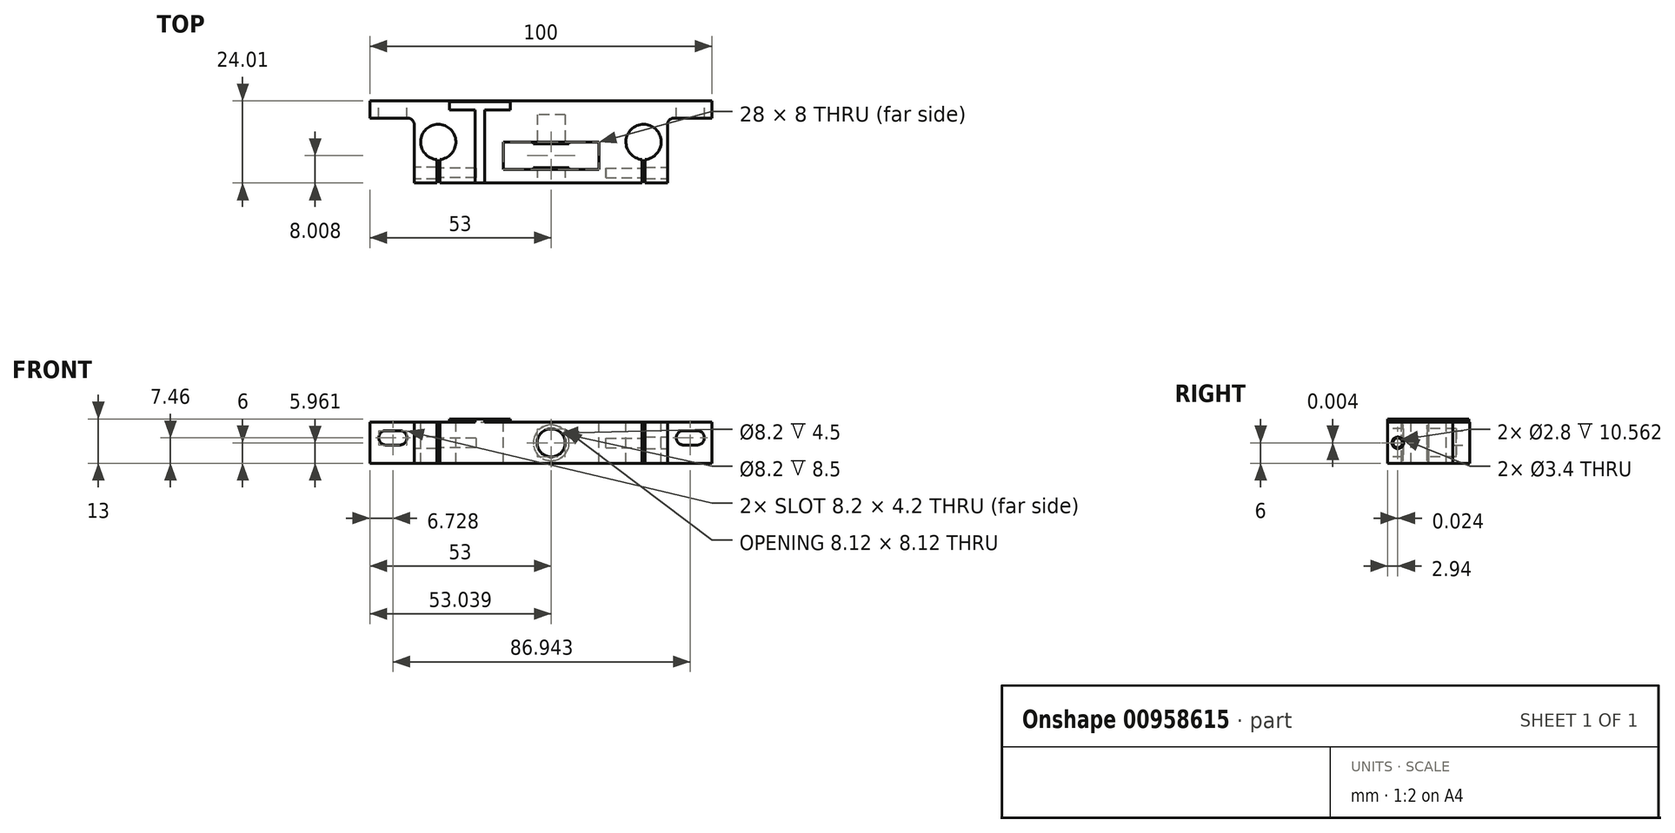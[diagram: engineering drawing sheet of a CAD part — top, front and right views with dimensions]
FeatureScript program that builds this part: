
annotation { "Feature Type Name" : "Feature", "Feature Type Description" : "" }
export const myFeature = defineFeature(function(context is Context, id is Id, definition is map)
    precondition{}
    {
        {
            var Q0;
            Q0=qCreatedBy(makeId("Top.planeOp"),FACE);
            var sketch = newSketch(context, id + "F0", { "sketchPlane" : qUnion([Q0])});
            skLineSegment(sketch, "E0", {"start": v(-46.35, 12.3) * mm, "end": v(53.65, 12.3) * mm});
            skLineSegment(sketch, "E1", {"start": v(53.65, 12.3) * mm, "end": v(53.65, 7.3) * mm});
            skLineSegment(sketch, "E2", {"start": v(53.65, 7.3) * mm, "end": v(40.65, 7.3) * mm});
            skLineSegment(sketch, "E3", {"start": v(40.65, 7.3) * mm, "end": v(40.65, -11.7) * mm});
            skLineSegment(sketch, "E4", {"start": v(40.65, -11.7) * mm, "end": v(-33.35, -11.7) * mm});
            skLineSegment(sketch, "E5", {"start": v(-33.35, -11.7) * mm, "end": v(-33.35, 7.3) * mm});
            skLineSegment(sketch, "E6", {"start": v(-33.35, 7.3) * mm, "end": v(-46.35, 7.3) * mm});
            skLineSegment(sketch, "E7", {"start": v(-46.35, 7.3) * mm, "end": v(-46.35, 12.3) * mm});
            skSolve(sketch);
        }
        {
            var Q0;
            Q0=qSketchRegion(id+"F0",true);
            extrude(context, id + "F1", {"entities" : qUnion([Q0]), "depth" : 12 * mm});
        }
        {
            var Q0;
            Q0=makeQuery(id+"F1.opExtrude","CAP_FACE",FACE,{"disambiguationData":[OSD([sQuery(id+"F0.wireOp",EDGE,"E0"),sQuery(id+"F0.wireOp",EDGE,"E1"),sQuery(id+"F0.wireOp",EDGE,"E2"),sQuery(id+"F0.wireOp",EDGE,"E3"),sQuery(id+"F0.wireOp",EDGE,"E4"),sQuery(id+"F0.wireOp",EDGE,"E5"),sQuery(id+"F0.wireOp",EDGE,"E6"),sQuery(id+"F0.wireOp",EDGE,"E7")])],"isStart":false});
            var sketch = newSketch(context, id + "F2", { "sketchPlane" : qUnion([Q0])});
            skCircle(sketch, "E8", {"center": v(-26.35, 0.3) * mm, "radius": 5.15 * mm});
            skCircle(sketch, "E9", {"center": v(33.65, 0.3) * mm, "radius": 5.15 * mm});
            skPoint(sketch, "E10", {"position": v(3.65, 12.3) * mm});
            skLineSegment(sketch, "E11.bottom", {"start": v(33.21, -3.01) * mm, "end": v(34.09, -3.01) * mm});
            skLineSegment(sketch, "E11.top", {"start": v(33.21, -12.27) * mm, "end": v(34.09, -12.27) * mm});
            skLineSegment(sketch, "E11.left", {"start": v(33.21, -3.01) * mm, "end": v(33.21, -12.27) * mm});
            skLineSegment(sketch, "E11.right", {"start": v(34.09, -3.01) * mm, "end": v(34.09, -12.27) * mm});
            skPoint(sketch, "E12", {"position": v(33.65, -3.01) * mm});
            skLineSegment(sketch, "E13", {"start": v(3.65, 12.3) * mm, "end": v(3.65, -11.7) * mm, "construction": true});
            skLineSegment(sketch, "E14.MirrorCS", {"start": v(-25.91, -12.27) * mm, "end": v(-26.79, -12.27) * mm});
            skLineSegment(sketch, "E15.MirrorCS", {"start": v(-26.79, -3.01) * mm, "end": v(-26.79, -12.27) * mm});
            skLineSegment(sketch, "E16.MirrorCS", {"start": v(-25.91, -3.01) * mm, "end": v(-26.79, -3.01) * mm});
            skLineSegment(sketch, "E17.MirrorCS", {"start": v(-25.91, -3.01) * mm, "end": v(-25.91, -12.27) * mm});
            skSolve(sketch);
        }
        {
            var Q0;
            Q0=qSketchRegion(id+"F2",true);
            var Q1;
            {var subQ3=sQuery(id+"F2.wireOp",EDGE,"E11.bottom");Q1=makeQuery(id+"F2.imprint","IMPRINT",FACE,{"disambiguationData":[TD([[makeQuery(id+"F2.imprint","IMPRINT",EDGE,{"derivedFrom":subQ3}),-1.0]])]});}
            var Q2;
            {var subQ3=sQuery(id+"F2.wireOp",EDGE,"E16.MirrorCS");Q2=makeQuery(id+"F2.imprint","IMPRINT",FACE,{"disambiguationData":[TD([[makeQuery(id+"F2.imprint","IMPRINT",EDGE,{"derivedFrom":subQ3}),1.0]])]});}
            extrude(context, id + "F3", {"entities" : qUnion([Q0, Q1, Q2]), "operationType" : NewBodyOperationType.REMOVE, "endBound" : BoundingType.THROUGH_ALL, "oppositeDirection" : true, "depth" : 25 * mm, "offsetDistance" : 25 * mm});
        }
        {
            var Q0;
            Q0=makeQuery(id+"F1.opExtrude","SWEPT_FACE",FACE,{"disambiguationData":[OSD([sQuery(id+"F0.wireOp",EDGE,"E0")])]});
            var sketch = newSketch(context, id + "F4", { "sketchPlane" : qUnion([Q0])});
            skLineSegment(sketch, "E18", {"start": v(-53.65, 7.46) * mm, "end": v(46.35, 7.46) * mm, "construction": true});
            skLineSegment(sketch, "E19.bottom", {"start": v(-49.32, 9.56) * mm, "end": v(-45.32, 9.56) * mm});
            skLineSegment(sketch, "E19.top", {"start": v(-49.32, 5.36) * mm, "end": v(-45.32, 5.36) * mm});
            skArc(sketch, "E20", {"start": v(-45.32, 5.36) * mm, "mid": v(-43.22, 7.46) * mm, "end": v(-45.32, 9.56) * mm});
            skArc(sketch, "E21", {"start": v(-49.32, 9.56) * mm, "mid": v(-51.42, 7.46) * mm, "end": v(-49.32, 5.36) * mm});
            skLineSegment(sketch, "E22.top", {"start": v(37.62, 5.36) * mm, "end": v(41.62, 5.36) * mm});
            skLineSegment(sketch, "E22.bottom", {"start": v(37.62, 9.56) * mm, "end": v(41.62, 9.56) * mm});
            skArc(sketch, "E23", {"start": v(37.62, 9.56) * mm, "mid": v(35.52, 7.46) * mm, "end": v(37.62, 5.36) * mm});
            skArc(sketch, "E24", {"start": v(41.62, 5.36) * mm, "mid": v(43.72, 7.46) * mm, "end": v(41.62, 9.56) * mm});
            skSolve(sketch);
        }
        {
            var Q0;
            Q0=qSketchRegion(id+"F4",true);
            extrude(context, id + "F5", {"entities" : qUnion([Q0]), "operationType" : NewBodyOperationType.REMOVE, "endBound" : BoundingType.THROUGH_ALL, "oppositeDirection" : true, "depth" : 25 * mm});
        }
        {
            var Q0;
            Q0=makeQuery(id+"F1.opExtrude","SWEPT_FACE",FACE,{"disambiguationData":[OSD([sQuery(id+"F0.wireOp",EDGE,"E4")])]});
            var sketch = newSketch(context, id + "F6", { "sketchPlane" : qUnion([Q0])});
            skLineSegment(sketch, "E25", {"start": v(-33.35, 6) * mm, "end": v(40.65, 6) * mm, "construction": true});
            skCircle(sketch, "E26", {"center": v(6.65, 6) * mm, "radius": 4.1 * mm});
            skSolve(sketch);
        }
        {
            var Q0;
            Q0=qSketchRegion(id+"F6",true);
            extrude(context, id + "F7", {"entities" : qUnion([Q0]), "operationType" : NewBodyOperationType.REMOVE, "oppositeDirection" : true, "depth" : 20 * mm});
        }
        {
            var Q0;
            Q0=makeQuery(id+"F1.opExtrude","CAP_FACE",FACE,{"disambiguationData":[OSD([sQuery(id+"F0.wireOp",EDGE,"E0"),sQuery(id+"F0.wireOp",EDGE,"E1"),sQuery(id+"F0.wireOp",EDGE,"E2"),sQuery(id+"F0.wireOp",EDGE,"E3"),sQuery(id+"F0.wireOp",EDGE,"E4"),sQuery(id+"F0.wireOp",EDGE,"E5"),sQuery(id+"F0.wireOp",EDGE,"E6"),sQuery(id+"F0.wireOp",EDGE,"E7")])],"isStart":false});
            var sketch = newSketch(context, id + "F8", { "sketchPlane" : qUnion([Q0])});
            skLineSegment(sketch, "E27.bottom", {"start": v(-7.35, 0.3) * mm, "end": v(20.65, 0.3) * mm});
            skLineSegment(sketch, "E27.top", {"start": v(-7.35, -7.7) * mm, "end": v(20.65, -7.7) * mm});
            skLineSegment(sketch, "E27.left", {"start": v(-7.35, 0.3) * mm, "end": v(-7.35, -7.7) * mm});
            skLineSegment(sketch, "E27.right", {"start": v(20.65, 0.3) * mm, "end": v(20.65, -7.7) * mm});
            skLineSegment(sketch, "E28", {"start": v(6.65, 12.3) * mm, "end": v(6.65, -11.7) * mm, "construction": true});
            skLineSegment(sketch, "E29", {"start": v(6.65, 0.3) * mm, "end": v(6.65, -7.7) * mm});
            skSolve(sketch);
        }
        {
            var Q0;
            Q0=qSketchRegion(id+"F8",true);
            extrude(context, id + "F9", {"entities" : qUnion([Q0]), "operationType" : NewBodyOperationType.REMOVE, "endBound" : BoundingType.THROUGH_ALL, "oppositeDirection" : true, "depth" : 25 * mm});
        }
        {
            var Q0;
            Q0=makeQuery(id+"F9.boolean.opBoolean","COPY",FACE,{"derivedFrom":makeQuery(id+"F9.opExtrude","SWEPT_FACE",FACE,{"disambiguationData":[OSD([sQuery(id+"F8.wireOp",EDGE,"E27.bottom")])]})});
            var sketch = newSketch(context, id + "F10", { "sketchPlane" : qUnion([Q0])});
            skCircle(sketch, "E30", {"center": v(6.65, 6) * mm, "radius": 5.2 * mm});
            skSolve(sketch);
        }
        {
            var Q0;
            Q0=makeQuery(id+"F10.imprint","IMPRINT",FACE,{"disambiguationData":[TD([[makeQuery(id+"F10.imprint","IMPRINT",EDGE,{"derivedFrom":sQuery(id+"F10.wireOp",EDGE,"E30")}),1.0]])]});
            extrude(context, id + "F11", {"entities" : qUnion([Q0]), "operationType" : NewBodyOperationType.ADD, "depth" : 0.5 * mm});
        }
        {
            var Q0;
            Q0=makeQuery(id+"F9.boolean.opBoolean","COPY",FACE,{"derivedFrom":makeQuery(id+"F9.opExtrude","SWEPT_FACE",FACE,{"disambiguationData":[OSD([sQuery(id+"F8.wireOp",EDGE,"E27.top")])]})});
            var sketch = newSketch(context, id + "F12", { "sketchPlane" : qUnion([Q0])});
            skCircle(sketch, "E31", {"center": v(-6.65, 6) * mm, "radius": 5.25 * mm});
            skSolve(sketch);
        }
        {
            var Q0;
            Q0=makeQuery(id+"F12.imprint","IMPRINT",FACE,{"disambiguationData":[TD([[makeQuery(id+"F12.imprint","IMPRINT",EDGE,{"derivedFrom":sQuery(id+"F12.wireOp",EDGE,"E31")}),1.0]])]});
            extrude(context, id + "F13", {"entities" : qUnion([Q0]), "operationType" : NewBodyOperationType.ADD, "depth" : 0.5 * mm});
        }
        {
            var Q0;
            Q0=makeQuery(id+"F1.opExtrude","CAP_FACE",FACE,{"disambiguationData":[OSD([sQuery(id+"F0.wireOp",EDGE,"E0"),sQuery(id+"F0.wireOp",EDGE,"E1"),sQuery(id+"F0.wireOp",EDGE,"E2"),sQuery(id+"F0.wireOp",EDGE,"E3"),sQuery(id+"F0.wireOp",EDGE,"E4"),sQuery(id+"F0.wireOp",EDGE,"E5"),sQuery(id+"F0.wireOp",EDGE,"E6"),sQuery(id+"F0.wireOp",EDGE,"E7")])],"isStart":false});
            var sketch = newSketch(context, id + "F14", { "sketchPlane" : qUnion([Q0])});
            skText(sketch, "E32", { "text": "T", "fontName": "OpenSans-Regular.ttf"});
            const initialGuessF14  = {"E32": [-0.02337, -0.0117, 1, 0, 0.024]};
            skSetInitialGuess(sketch, initialGuessF14);
            skSolve(sketch);
        }
        {
            var Q0;
            Q0=qSketchRegion(id+"F14",true);
            extrude(context, id + "F15", {"entities" : qUnion([Q0]), "operationType" : NewBodyOperationType.ADD, "depth" : 1 * mm});
        }
        {
            var Q0;
            Q0=makeQuery(id+"F1.opExtrude","SWEPT_FACE",FACE,{"disambiguationData":[OSD([sQuery(id+"F0.wireOp",EDGE,"E3")])]});
            var sketch = newSketch(context, id + "F16", { "sketchPlane" : qUnion([Q0])});
            skCircle(sketch, "E33", {"center": v(-8.74, 6) * mm, "radius": 1.7 * mm});
            skCircle(sketch, "E34", {"center": v(-8.74, 6) * mm, "radius": 1.4 * mm});
            skLineSegment(sketch, "E35", {"start": v(-11.7, 6) * mm, "end": v(-3.84, 6) * mm, "construction": true});
            skSolve(sketch);
        }
        {
            var Q0;
            Q0=makeQuery(id+"F16.imprint","IMPRINT",FACE,{"disambiguationData":[TD([[makeQuery(id+"F16.imprint","IMPRINT",EDGE,{"derivedFrom":sQuery(id+"F16.wireOp",EDGE,"E34")}),1.0]])]});
            extrude(context, id + "F17", {"entities" : qUnion([Q0]), "operationType" : NewBodyOperationType.REMOVE, "oppositeDirection" : true, "depth" : 18 * mm});
        }
        {
            var Q0;
            Q0=makeQuery(id+"F16.imprint","IMPRINT",FACE,{"disambiguationData":[TD([[makeQuery(id+"F16.imprint","IMPRINT",EDGE,{"derivedFrom":sQuery(id+"F16.wireOp",EDGE,"E34")}),1.0]])]});
            var Q1;
            Q1=makeQuery(id+"F16.imprint","IMPRINT",FACE,{"disambiguationData":[TD([[makeQuery(id+"F16.imprint","IMPRINT",EDGE,{"derivedFrom":sQuery(id+"F16.wireOp",EDGE,"E33")}),1.0]])]});
            extrude(context, id + "F18", {"entities" : qUnion([Q0, Q1]), "operationType" : NewBodyOperationType.REMOVE, "endBound" : BoundingType.UP_TO_NEXT, "oppositeDirection" : true, "depth" : 7 * mm});
        }
        {
            var Q0;
            Q0=makeQuery(id+"F1.opExtrude","SWEPT_EDGE",EDGE,{"disambiguationData":[OSD([sQuery(id+"F0.wireOp",EDGE,"E2"),sQuery(id+"F0.wireOp",EDGE,"E3")])]});
            fillet(context, id + "F19", {"entities" : qUnion([Q0]), "radius" : 2 * mm, "tangentPropagation" : true, "allowEdgeOverflow" : false});
        }
        {
            var Q0;
            Q0=makeQuery(id+"F1.opExtrude","SWEPT_FACE",FACE,{"disambiguationData":[OSD([sQuery(id+"F0.wireOp",EDGE,"E5")])]});
            var sketch = newSketch(context, id + "F20", { "sketchPlane" : qUnion([Q0])});
            skCircle(sketch, "E36", {"center": v(8.76, 6) * mm, "radius": 1.7 * mm});
            skCircle(sketch, "E37", {"center": v(8.76, 6) * mm, "radius": 1.4 * mm});
            skLineSegment(sketch, "E38", {"start": v(8.76, 0) * mm, "end": v(8.76, 12) * mm, "construction": true});
            skSolve(sketch);
        }
        {
            var Q0;
            Q0=makeQuery(id+"F20.imprint","IMPRINT",FACE,{"disambiguationData":[TD([[makeQuery(id+"F20.imprint","IMPRINT",EDGE,{"derivedFrom":sQuery(id+"F20.wireOp",EDGE,"E37")}),1.0]])]});
            extrude(context, id + "F21", {"entities" : qUnion([Q0]), "operationType" : NewBodyOperationType.REMOVE, "oppositeDirection" : true, "depth" : 18 * mm});
        }
        {
            var Q0;
            Q0=makeQuery(id+"F20.imprint","IMPRINT",FACE,{"disambiguationData":[TD([[makeQuery(id+"F20.imprint","IMPRINT",EDGE,{"derivedFrom":sQuery(id+"F20.wireOp",EDGE,"E37")}),1.0]])]});
            var Q1;
            Q1=makeQuery(id+"F20.imprint","IMPRINT",FACE,{"disambiguationData":[TD([[makeQuery(id+"F20.imprint","IMPRINT",EDGE,{"derivedFrom":sQuery(id+"F20.wireOp",EDGE,"E36")}),1.0]])]});
            extrude(context, id + "F22", {"entities" : qUnion([Q0, Q1]), "operationType" : NewBodyOperationType.REMOVE, "endBound" : BoundingType.UP_TO_NEXT, "oppositeDirection" : true, "depth" : 25 * mm});
        }
        {
            var Q0;
            Q0=makeQuery(id+"F1.opExtrude","SWEPT_EDGE",EDGE,{"disambiguationData":[OSD([sQuery(id+"F0.wireOp",EDGE,"E5"),sQuery(id+"F0.wireOp",EDGE,"E6")])]});
            fillet(context, id + "F23", {"entities" : qUnion([Q0]), "radius" : 2 * mm, "tangentPropagation" : true, "allowEdgeOverflow" : false});
        }
    });
